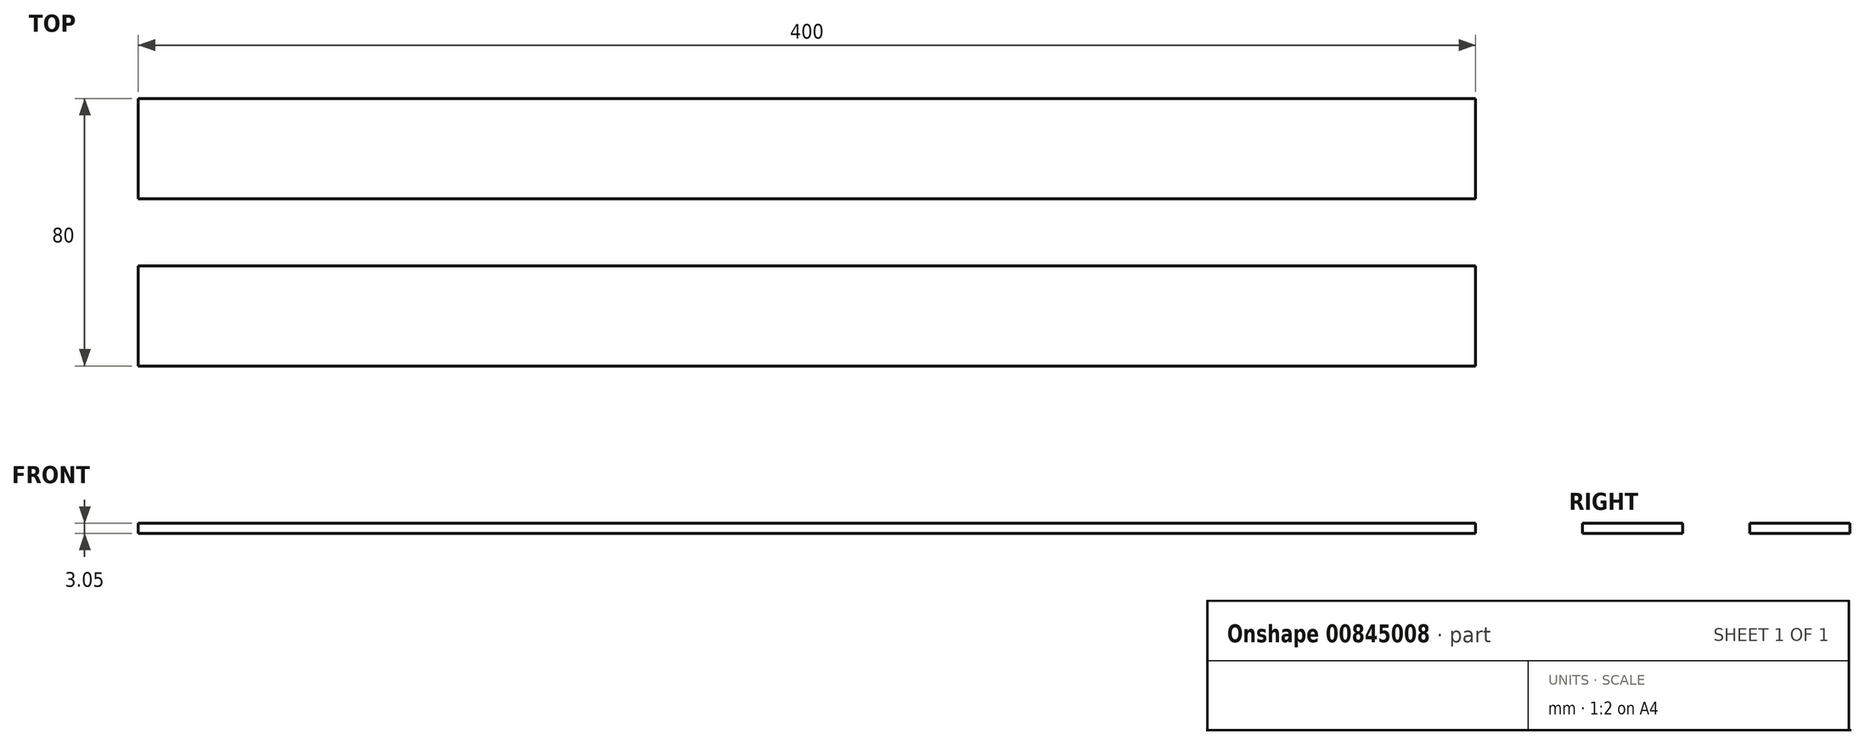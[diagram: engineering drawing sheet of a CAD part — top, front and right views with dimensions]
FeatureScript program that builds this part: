
annotation { "Feature Type Name" : "Feature", "Feature Type Description" : "" }
export const myFeature = defineFeature(function(context is Context, id is Id, definition is map)
    precondition{}
    {
        {
            var Q0;
            Q0=qCreatedBy(makeId("Top.planeOp"),FACE);
            var sketch = newSketch(context, id + "F0", { "sketchPlane" : qUnion([Q0])});
            skLineSegment(sketch, "E0", {"start": v(0, 0) * mm, "end": v(-400, 0) * mm});
            skLineSegment(sketch, "E1", {"start": v(-400, 0) * mm, "end": v(-400, 30) * mm});
            skLineSegment(sketch, "E2", {"start": v(-400, 30) * mm, "end": v(0, 30) * mm});
            skLineSegment(sketch, "E3", {"start": v(0, 30) * mm, "end": v(0, 0) * mm});
            skLineSegment(sketch, "E4", {"start": v(0, 50) * mm, "end": v(0, 80) * mm});
            skLineSegment(sketch, "E5", {"start": v(0, 80) * mm, "end": v(-400, 80) * mm});
            skLineSegment(sketch, "E6", {"start": v(-400, 80) * mm, "end": v(-400, 50) * mm});
            skLineSegment(sketch, "E7", {"start": v(-400, 50) * mm, "end": v(0, 50) * mm});
            skSolve(sketch);
        }
        {
            var Q0;
            Q0 = qSketchRegion(id + "F0", true);
            extrude(context, id + "F1", {"entities" : qUnion([Q0]), "depth" : 3.05 * mm, "offsetDistance" : 25.4 * mm});
        }
    });
